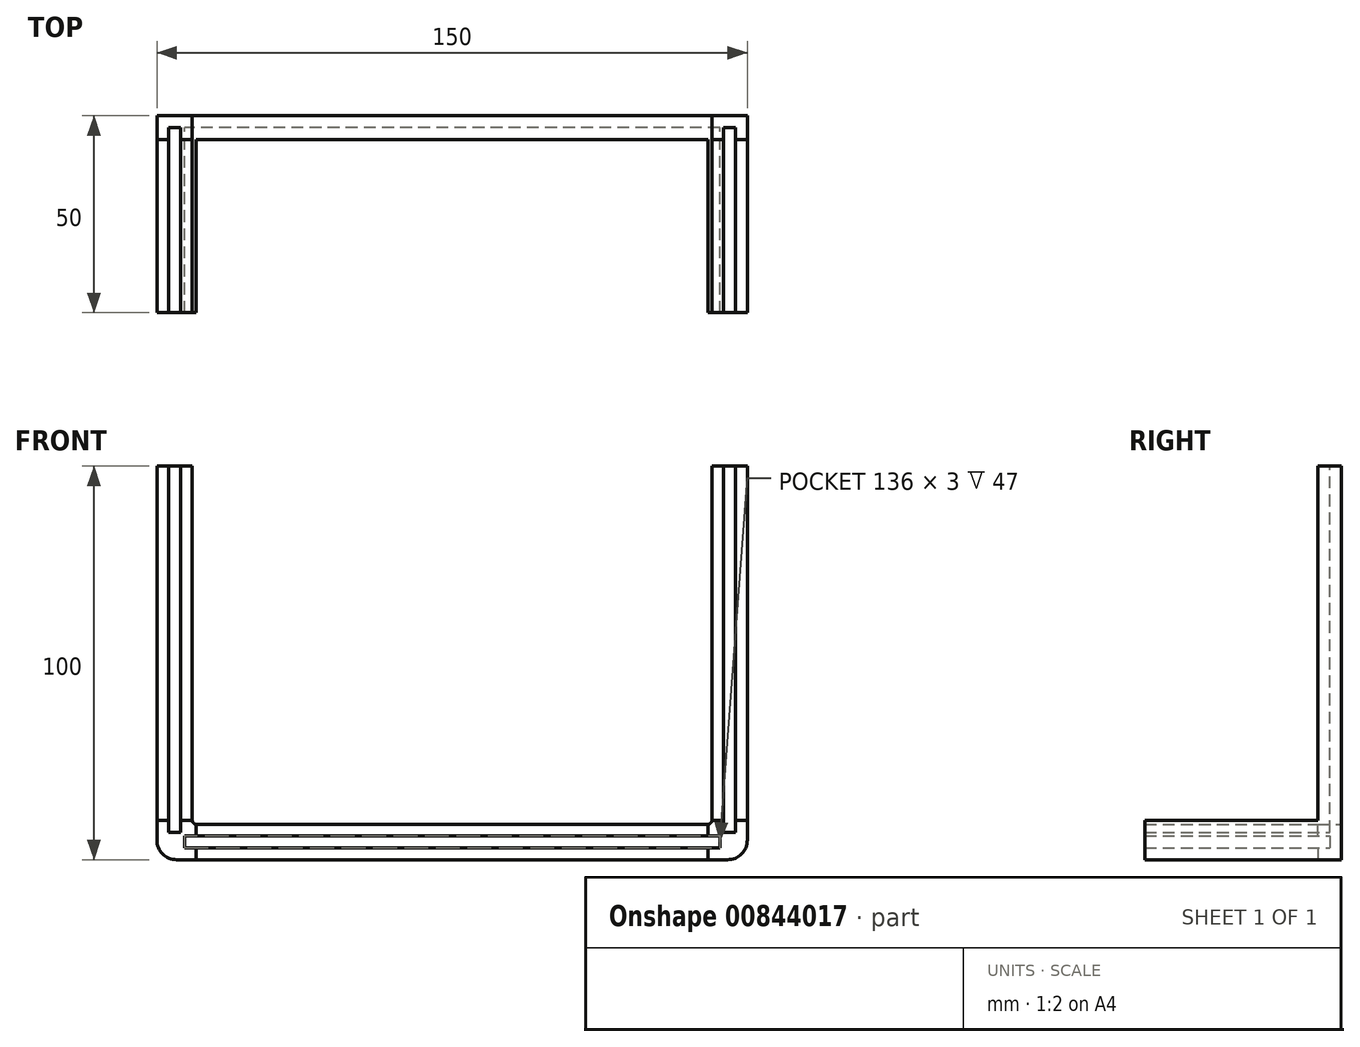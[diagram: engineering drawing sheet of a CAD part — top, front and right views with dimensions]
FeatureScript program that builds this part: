
annotation { "Feature Type Name" : "Feature", "Feature Type Description" : "" }
export const myFeature = defineFeature(function(context is Context, id is Id, definition is map)
    precondition{}
    {
        {
            var Q0;
            Q0=qCreatedBy(makeId("Front.planeOp"),FACE);
            var sketch = newSketch(context, id + "F0", { "sketchPlane" : qUnion([Q0])});
            skLineSegment(sketch, "E0", {"start": v(0, 0) * mm, "end": v(-75, 0) * mm});
            skLineSegment(sketch, "E1", {"start": v(-75, 0) * mm, "end": v(-75, 100) * mm});
            skLineSegment(sketch, "E2", {"start": v(0, 0) * mm, "end": v(0, 9) * mm});
            skLineSegment(sketch, "E3", {"start": v(0, 9) * mm, "end": v(-66, 9) * mm});
            skLineSegment(sketch, "E4", {"start": v(-66, 9) * mm, "end": v(-66, 100) * mm});
            skLineSegment(sketch, "E5", {"start": v(-66, 100) * mm, "end": v(-75, 100) * mm});
            skLineSegment(sketch, "E6.0", {"start": v(0, 3) * mm, "end": v(-72, 3) * mm});
            skLineSegment(sketch, "E7.0", {"start": v(-72, 3) * mm, "end": v(-72, 100) * mm});
            skLineSegment(sketch, "E8.0", {"start": v(0, 6) * mm, "end": v(-67, 6) * mm});
            skLineSegment(sketch, "E9.0", {"start": v(-69, 9) * mm, "end": v(-69, 100) * mm});
            skLineSegment(sketch, "E10", {"start": v(-69, 9) * mm, "end": v(-69, 6) * mm});
            skLineSegment(sketch, "E11", {"start": v(-67, 6) * mm, "end": v(-69, 6) * mm});
            skLineSegment(sketch, "E12.0", {"start": v(-68, 6) * mm, "end": v(-68, 3) * mm});
            skLineSegment(sketch, "E13.0", {"start": v(-69, 7) * mm, "end": v(-72, 7) * mm});
            skPoint(sketch, "E14.start.orphan", {"position": v(-66, 6) * mm});
            skLineSegment(sketch, "E15", {"start": v(-69, 10) * mm, "end": v(-66, 10) * mm});
            skLineSegment(sketch, "E16", {"start": v(-72, 10) * mm, "end": v(-75, 10) * mm});
            skLineSegment(sketch, "E17", {"start": v(-65, 6) * mm, "end": v(-65, 9) * mm});
            skLineSegment(sketch, "E18", {"start": v(-65, 3) * mm, "end": v(-65, 0) * mm});
            skSolve(sketch);
        }
        {
            var Q0;
            {var subQ3=sQuery(id+"F0.wireOp",EDGE,"E15");Q0=makeQuery(id+"F0.imprint","IMPRINT",FACE,{"disambiguationData":[TD([[makeQuery(id+"F0.imprint","IMPRINT",EDGE,{"derivedFrom":subQ3}),-1.0]])]});}
            var Q1;
            {var subQ4=sQuery(id+"F0.wireOp",EDGE,"E12.0");Q1=makeQuery(id+"F0.imprint","IMPRINT",FACE,{"disambiguationData":[TD([[makeQuery(id+"F0.imprint","IMPRINT",EDGE,{"derivedFrom":subQ4}),-1.0]])]});}
            var Q2;
            {var subQ6=sQuery(id+"F0.wireOp",EDGE,"E16");Q2=makeQuery(id+"F0.imprint","IMPRINT",FACE,{"disambiguationData":[TD([[makeQuery(id+"F0.imprint","IMPRINT",EDGE,{"derivedFrom":subQ6}),1.0]])]});}
            extrude(context, id + "F1", {"entities" : qUnion([Q0, Q1, Q2]), "depth" : 50 * mm, "offsetDistance" : 25 * mm});
        }
        {
            var Q0;
            {var subQ3=sQuery(id+"F0.wireOp",EDGE,"E16");Q0=makeQuery(id+"F0.imprint","IMPRINT",FACE,{"disambiguationData":[TD([[makeQuery(id+"F0.imprint","IMPRINT",EDGE,{"derivedFrom":subQ3}),-1.0]])]});}
            var Q1;
            {var subQ3=sQuery(id+"F0.wireOp",EDGE,"E15");Q1=makeQuery(id+"F0.imprint","IMPRINT",FACE,{"disambiguationData":[TD([[makeQuery(id+"F0.imprint","IMPRINT",EDGE,{"derivedFrom":subQ3}),1.0]])]});}
            var Q2;
            {var subQ5=sQuery(id+"F0.wireOp",EDGE,"E17");Q2=makeQuery(id+"F0.imprint","IMPRINT",FACE,{"disambiguationData":[TD([[makeQuery(id+"F0.imprint","IMPRINT",EDGE,{"derivedFrom":subQ5}),-1.0]])]});}
            var Q3;
            {var subQ3=sQuery(id+"F0.wireOp",EDGE,"E18");Q3=makeQuery(id+"F0.imprint","IMPRINT",FACE,{"disambiguationData":[TD([[makeQuery(id+"F0.imprint","IMPRINT",EDGE,{"derivedFrom":subQ3}),1.0]])]});}
            extrude(context, id + "F2", {"entities" : qUnion([Q0, Q1, Q2, Q3]), "operationType" : NewBodyOperationType.ADD, "depth" : 6 * mm, "offsetDistance" : 25 * mm});
        }
        {
            var Q0;
            {var subQ4=sQuery(id+"F0.wireOp",EDGE,"E13.0");Q0=makeQuery(id+"F0.imprint","IMPRINT",FACE,{"disambiguationData":[TD([[makeQuery(id+"F0.imprint","IMPRINT",EDGE,{"derivedFrom":subQ4}),-1.0]])]});}
            var Q1;
            {var subQ7=sQuery(id+"F0.wireOp",EDGE,"E12.0");Q1=makeQuery(id+"F0.imprint","IMPRINT",FACE,{"disambiguationData":[TD([[makeQuery(id+"F0.imprint","IMPRINT",EDGE,{"derivedFrom":subQ7}),1.0]])]});}
            extrude(context, id + "F3", {"entities" : qUnion([Q0, Q1]), "operationType" : NewBodyOperationType.ADD, "depth" : 3 * mm, "offsetDistance" : 25 * mm});
        }
        {
            var Q0;
            Q0=makeQuery(id+"F1.opExtrude","SWEPT_EDGE",EDGE,{"disambiguationData":[OSD([sQuery(id+"F0.wireOp",EDGE,"E3"),sQuery(id+"F0.wireOp",EDGE,"E4")])]});
            fillet(context, id + "F4", {"entities" : qUnion([Q0]), "radius" : 1 * mm, "tangentPropagation" : true, "allowEdgeOverflow" : false});
        }
        {
            var Q0;
            Q0=makeQuery(id+"F1.opExtrude","SWEPT_EDGE",EDGE,{"disambiguationData":[OSD([sQuery(id+"F0.wireOp",EDGE,"E0"),sQuery(id+"F0.wireOp",EDGE,"E1")])]});
            fillet(context, id + "F5", {"entities" : qUnion([Q0]), "radius" : 5 * mm, "tangentPropagation" : true, "allowEdgeOverflow" : false});
        }
        {
            var Q0;
            Q0=makeQuery(id+"F1.opExtrude","SWEPT_BODY",BODY,{"disambiguationData":[OSD([sQuery(id+"F0.wireOp",EDGE,"E0"),sQuery(id+"F0.wireOp",EDGE,"E1"),sQuery(id+"F0.wireOp",EDGE,"E3"),sQuery(id+"F0.wireOp",EDGE,"E4"),sQuery(id+"F0.wireOp",EDGE,"E6.0"),sQuery(id+"F0.wireOp",EDGE,"E7.0"),sQuery(id+"F0.wireOp",EDGE,"E8.0"),sQuery(id+"F0.wireOp",EDGE,"E9.0"),sQuery(id+"F0.wireOp",EDGE,"E10"),sQuery(id+"F0.wireOp",EDGE,"E11"),sQuery(id+"F0.wireOp",EDGE,"E12.0"),sQuery(id+"F0.wireOp",EDGE,"E13.0"),sQuery(id+"F0.wireOp",EDGE,"E15"),sQuery(id+"F0.wireOp",EDGE,"E16"),sQuery(id+"F0.wireOp",EDGE,"E17"),sQuery(id+"F0.wireOp",EDGE,"E18")])]});
            var Q1;
            Q1=qCreatedBy(makeId("Right.planeOp"),FACE);
            mirror(context, id + "F6", {"operationType" : NewBodyOperationType.ADD, "entities" : qUnion([Q0]), "mirrorPlane" : qUnion([Q1])});
        }
    });
